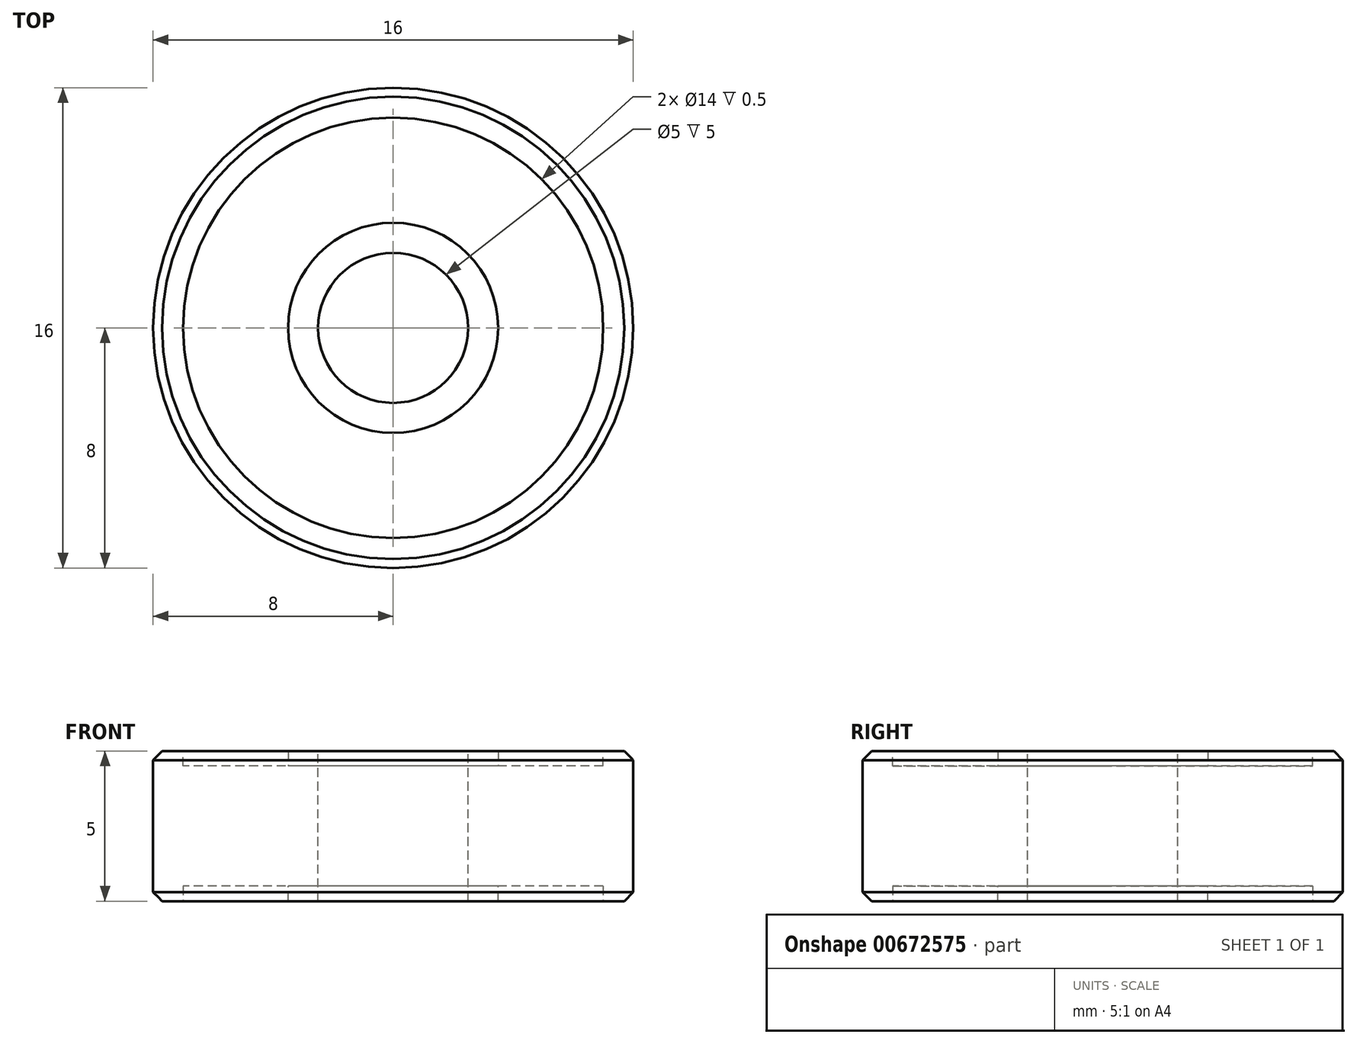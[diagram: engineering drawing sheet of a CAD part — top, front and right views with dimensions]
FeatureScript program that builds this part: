
annotation { "Feature Type Name" : "Feature", "Feature Type Description" : "" }
export const myFeature = defineFeature(function(context is Context, id is Id, definition is map)
    precondition{}
    {
        {
            var Q0;
            Q0=qCreatedBy(makeId("Top.planeOp"),FACE);
            var sketch = newSketch(context, id + "F0", { "sketchPlane" : qUnion([Q0])});
            skCircle(sketch, "E0", {"center": v(0, 0) * mm, "radius": 8 * mm});
            skSolve(sketch);
        }
        {
            var Q0;
            Q0=makeQuery(id+"F0.imprint","IMPRINT",FACE,{"disambiguationData":[TD([[makeQuery(id+"F0.imprint","IMPRINT",EDGE,{"derivedFrom":sQuery(id+"F0.wireOp",EDGE,"E0")}),1.0]])]});
            extrude(context, id + "F1", {"entities" : qUnion([Q0]), "depth" : 2.5 * mm, "offsetDistance" : 25 * mm});
        }
        {
            var Q0;
            Q0=makeQuery(id+"F1.opExtrude","CAP_FACE",FACE,{"disambiguationData":[OSD([sQuery(id+"F0.wireOp",EDGE,"E0")])],"isStart":false});
            var sketch = newSketch(context, id + "F2", { "sketchPlane" : qUnion([Q0])});
            skCircle(sketch, "E1", {"center": v(0, 0) * mm, "radius": 7 * mm});
            skSolve(sketch);
        }
        {
            var Q0;
            Q0=makeQuery(id+"F2.imprint","IMPRINT",FACE,{"disambiguationData":[TD([[makeQuery(id+"F2.imprint","IMPRINT",EDGE,{"derivedFrom":sQuery(id+"F2.wireOp",EDGE,"E1")}),1.0]])]});
            extrude(context, id + "F3", {"entities" : qUnion([Q0]), "operationType" : NewBodyOperationType.REMOVE, "oppositeDirection" : true, "depth" : 0.5 * mm, "offsetDistance" : 25 * mm});
        }
        {
            var Q0;
            Q0=makeQuery(id+"F3.boolean.opBoolean","COPY",FACE,{"derivedFrom":makeQuery(id+"F3.opExtrude","CAP_FACE",FACE,{"disambiguationData":[OSD([sQuery(id+"F2.wireOp",EDGE,"E1")])],"isStart":false})});
            var sketch = newSketch(context, id + "F4", { "sketchPlane" : qUnion([Q0])});
            skCircle(sketch, "E2", {"center": v(0, 0) * mm, "radius": 3.5 * mm});
            skSolve(sketch);
        }
        {
            var Q0;
            Q0=makeQuery(id+"F4.imprint","IMPRINT",FACE,{"disambiguationData":[TD([[makeQuery(id+"F4.imprint","IMPRINT",EDGE,{"derivedFrom":sQuery(id+"F4.wireOp",EDGE,"E2")}),1.0]])]});
            extrude(context, id + "F5", {"entities" : qUnion([Q0]), "operationType" : NewBodyOperationType.ADD, "depth" : 0.5 * mm, "offsetDistance" : 25 * mm});
        }
        {
            var Q0;
            Q0=makeQuery(id+"F5.opExtrude","CAP_FACE",FACE,{"disambiguationData":[OSD([sQuery(id+"F4.wireOp",EDGE,"E2")])],"isStart":false});
            var sketch = newSketch(context, id + "F6", { "sketchPlane" : qUnion([Q0])});
            skCircle(sketch, "E3", {"center": v(0, 0) * mm, "radius": 2.5 * mm});
            skSolve(sketch);
        }
        {
            var Q0;
            Q0=makeQuery(id+"F6.imprint","IMPRINT",FACE,{"disambiguationData":[TD([[makeQuery(id+"F6.imprint","IMPRINT",EDGE,{"derivedFrom":sQuery(id+"F6.wireOp",EDGE,"E3")}),1.0]])]});
            extrude(context, id + "F7", {"entities" : qUnion([Q0]), "operationType" : NewBodyOperationType.REMOVE, "oppositeDirection" : true, "depth" : 25 * mm, "offsetDistance" : 25 * mm});
        }
        {
            var Q0;
            Q0=makeQuery(id+"F1.opExtrude","SWEPT_BODY",BODY,{"disambiguationData":[OSD([sQuery(id+"F0.wireOp",EDGE,"E0")])]});
            var Q1;
            Q1=makeQuery(id+"F1.opExtrude","CAP_FACE",FACE,{"disambiguationData":[OSD([sQuery(id+"F0.wireOp",EDGE,"E0")])],"isStart":true});
            mirror(context, id + "F8", {"operationType" : NewBodyOperationType.ADD, "entities" : qUnion([Q0]), "mirrorPlane" : qUnion([Q1])});
        }
        {
            var Q0;
            Q0=makeQuery(id+"F1.opExtrude","CAP_EDGE",EDGE,{"disambiguationData":[OSD([sQuery(id+"F0.wireOp",EDGE,"E0")])],"isStart":false});
            var Q1;
            Q1=makeQuery(id+"F8.opPattern","COPY",EDGE,{"derivedFrom":makeQuery(id+"F1.opExtrude","CAP_EDGE",EDGE,{"disambiguationData":[OSD([sQuery(id+"F0.wireOp",EDGE,"E0")])],"isStart":false}),"instanceName":"1"});
            chamfer(context, id + "F9", {"entities" : qUnion([Q0, Q1]), "width" : 0.3 * mm, "tangentPropagation" : true});
        }
    });
